# Revit family: Speaker-Ceiling-TOA-F-122 clean
name_source: partatom
category: Communication Devices
revit_build: Autodesk Revit 2013 (Build: 20130531_2115(x64)
units: mm (PartAtom-declared; Revit-internal decimal feet)

## types (1)
- 5"
    25V Taps = 3.7W, 1.9W, 0.6W, 0.2W & 0.06W
    70V Taps = 30W, 15W, 5W, 1.5W & 0.5W
    Assembly Code = E1020300
    Body Diameter = 7.874 "
    Body Radius = 3.937 "
    Clip Length = 0.5 "
    Coverage Horizontal = 180.00°
    Coverage Vertical = 180.00°
    Default Elevation = 48 "
    Description = FULL-RANGE PROCESSED CEILING SPEAKER (5”)
    Enclosure Material = Metal - TOA - Steel Plate
    Grille Diameter = 9.055 "
    Grille Height = 1.614 "
    Grille Material = Mesh - TOA - White
    Grille Radius = 4.528 "
    Height = 8.701 "
    Highlight Material = Paint - TOA - White
    IQ Category = Speaker
    Length 1 = 4.409 "
    Load Classification = Other
    Long Term Power Handling = 120 W
    Manufacturer = TOA Electronics Inc.
    Manufacturer URL = http://www.toaelectronics.com
    Maximum Ceiling Thickness = 1.457 "
    Model = F-122CU
    Mounting Options = Ceiling Reinforcement Ring, Tile Bridge, Trim Ring, Surface Back-Can & Safety Wire
    Offset = 0 "
    Operating Weight = 8.16 lb
    Product Documentation Link = http://www.toaelectronics.com
    Product Name = F-122CU
    Product Page URL = http://www.toaelectronics.com
    Regulatory Compliance = UL
    SPL Measurement Bandwidth = 70 to 20kHz
    Sensitivity = 90
    Transformer Option = Yes
    Type Comments = F-122CU
    URL = http://www.toaelectronics.com
    Weight Product = 8.16
    Width = 9.055 "

## geometry (parser evidence)
native form markers: Blend x1, Sweep x4
no freeform markers — native parametric forms only
